# Revit family: KS Husky, Typ IV-19, M10-M12, Ø 88,9-114,3
name_source: partatom
category: HLS-Bauteile
revit_build: Autodesk Revit 2017 (Build: 20190507_1515(x64)
units: mm (PartAtom-declared; Revit-internal decimal feet)

## family parameters
Arbeitsebenenbasiert = Ja
Beim Laden mit Abzugskörper schneiden = Nein
Bemaßung runder Anschluss = Durchmesser verwenden
Gemeinsam genutzt = Ja
Immer vertikal = Nein
Raumberechnungspunkt = Nein
Teiletyp = Normal

## types (4) — shared parameters
Anschluss = M10/M12
Baustoffklasse = B2
DVS = 5 mm  [stored 0.0164042 ft]
Dichte Kern = 120 kg/m³
Dämmkörper = KA/PU
Fabrikat = MEFA
Firma = MEFA Befestigungs- und Montagesysteme GmbH
H1 = 2 mm  [stored 0.00656168 ft]
H2 = 4 mm  [stored 0.0131234 ft]
HGA = 22 mm  [stored 0.0721785 ft]
Kurztext1 = Kälteschelle Husky IV 19
L = 42 mm  [stored 0.137795 ft]
MB = 25 mm  [stored 0.082021 ft]
MD = 3 mm  [stored 0.00984252 ft]
Material = Stahl
Material Mantel = Kunststoff
Materialname = DD11
Mengeneinheit = St
Oberflaeche = galvanisch verzinkt
Rohrschellentyp = Trabant
Schalenlänge = 42 mm
Typ = IV 19
Vorgabe-Ansicht = 1219 mm
Wasserdampfdiffusionswiderstand = 7000 µ
Wärmeleitfähigkeit = 0.029 W/mK
max. Temperaturbeständigkeit = 105 °C
mittl. Nenndruckfestigkeit Kern = 1,35 N/mm²
stat. Belastung Kern = 0,27 N/mm²

## per-type parameters (varying)
| type | A | Anschlußhöhe | Artikelnummer | B | Breite | D | D0 | DF1 | DF2 | DS | Dämmstärke | EAN | Gewicht | Gewicht pro Bauteil | H | Kurztext2 | R | RM | Rohraußendurchmesser Kunststoff | Rohraußendurchmesser Stahl | S | max. zul. Last | vpe |
| Kälteschelle Husky, Typ IV-19, M10/M12, Ø 88,9 | 51 mm | 43 mm | 6840891 | 187 mm  [stored 0.613517 ft] | 187 mm  [stored 0.613517 ft] | 89 mm | 142 mm | 20 mm  [stored 0.0656168 ft] | 20 mm  [stored 0.0656168 ft] | 27 mm  [stored 0.0885827 ft] | 27 mm  [stored 0.0885827 ft] | 4250928440853 | 0.37 kg | 0.37 kg | 169 mm | 88,9 mm Iso 27 x 42 mm M10/M12 | 71 mm | 74 mm |  | 88,9 mm | 167 mm | 0.88 kN | 8 St |
| Kälteschelle Husky, Typ IV-19, M10/M12, Ø108 | 54 mm | 53 mm | 6841081 | 215 mm | 215 mm | 108 mm  [stored 0.354331 ft] | 166 mm  [stored 0.544619 ft] | 22 mm  [stored 0.0721785 ft] | 22 mm  [stored 0.0721785 ft] | 29 mm  [stored 0.0951444 ft] | 29 mm  [stored 0.0951444 ft] | 4250928440860 | 0.42 kg | 0.42 kg | 193 mm  [stored 0.633202 ft] | 108 mm Iso 29 x 42 mm M10/M12 | 83 mm  [stored 0.27231 ft] | 86 mm |  | 108 mm | 193 mm  [stored 0.633202 ft] | 1.07 kN | 4 St |
| Kälteschelle Husky, Typ IV-19, M10/M12, Ø110 | 53 mm | 52 mm | 6841101 | 215 mm | 215 mm | 110 mm  [stored 0.360892 ft] | 166 mm  [stored 0.544619 ft] | 22 mm  [stored 0.0721785 ft] | 22 mm  [stored 0.0721785 ft] | 28 mm  [stored 0.0918635 ft] | 28 mm  [stored 0.0918635 ft] | 4250928440877 | 0.42 kg | 0.42 kg | 193 mm  [stored 0.633202 ft] | 110 mm Iso 28 x 42 mm M10/M12 | 83 mm  [stored 0.27231 ft] | 86 mm | 110 mm |  | 193 mm  [stored 0.633202 ft] | 1.09 kN | 4 St |
| Kälteschelle Husky, Typ IV-19, M10/M12, Ø114,3 | 50 mm  [stored 0.164042 ft] | 50 mm | 6841141 | 215 mm | 215 mm | 114 mm | 166 mm  [stored 0.544619 ft] | 22 mm  [stored 0.0721785 ft] | 22 mm  [stored 0.0721785 ft] | 26 mm | 26 mm | 4250928440884 | 0.42 kg | 0.42 kg | 193 mm  [stored 0.633202 ft] | 114,3 mm Iso 26 x 42 mm M10/M12 | 83 mm  [stored 0.27231 ft] | 86 mm |  | 114,3 mm | 193 mm  [stored 0.633202 ft] | 1.13 kN | 4 St |

note: [stored X ft] marks values corroborated as IEEE doubles in the binary element streams (Revit-internal decimal feet)

## geometry (parser evidence)
native form markers: Sweep x3
no freeform markers — native parametric forms only
